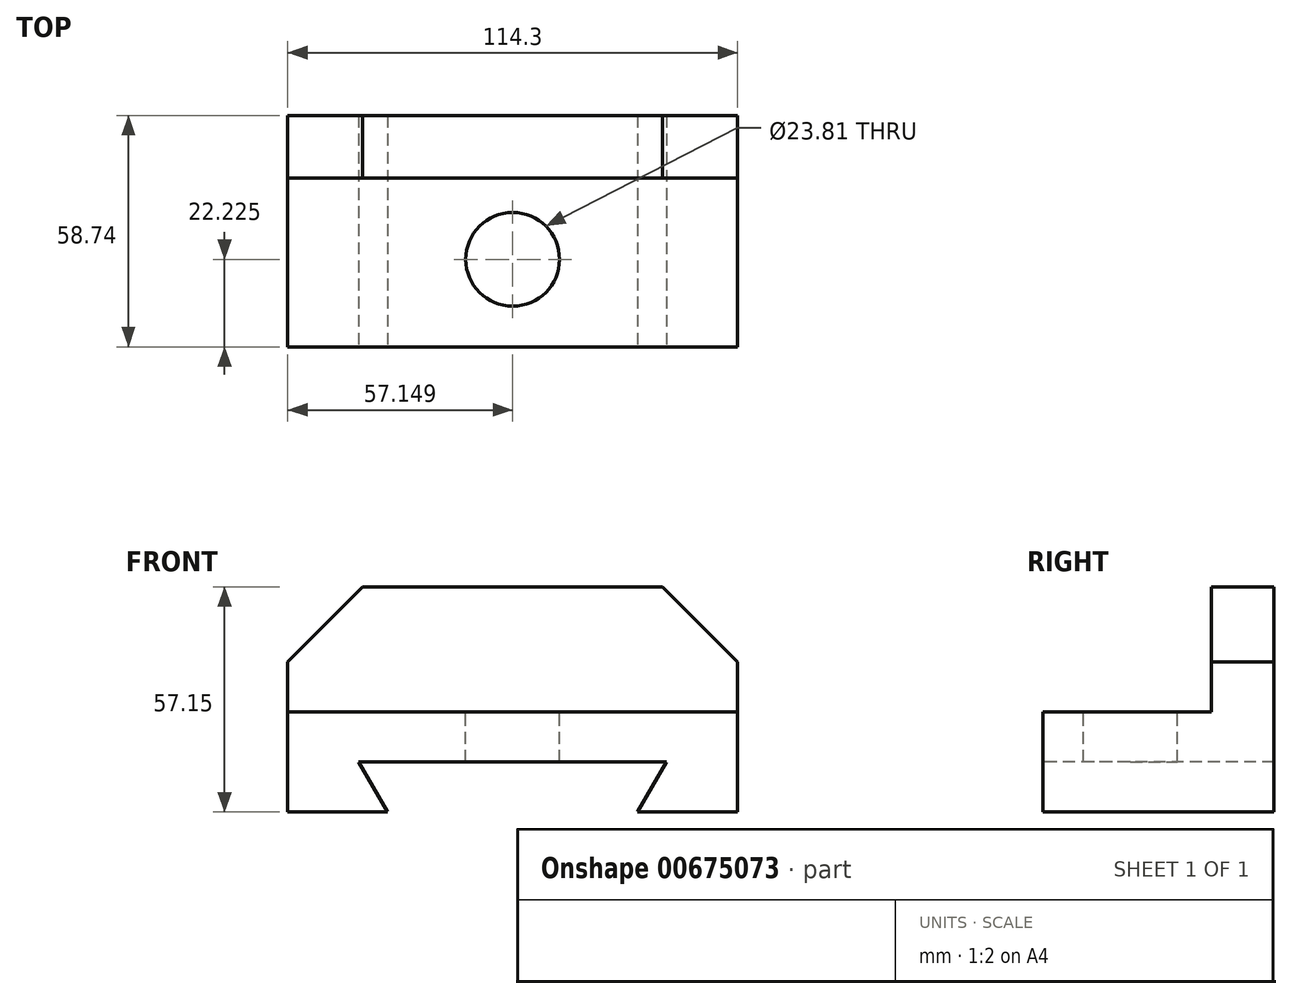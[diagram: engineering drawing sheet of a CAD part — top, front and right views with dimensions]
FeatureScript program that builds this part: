
annotation { "Feature Type Name" : "Feature", "Feature Type Description" : "" }
export const myFeature = defineFeature(function(context is Context, id is Id, definition is map)
    precondition{}
    {
        {
            var Q0;
            Q0=qCreatedBy(makeId("Front.planeOp"),FACE);
            var sketch = newSketch(context, id + "F0", { "sketchPlane" : qUnion([Q0])});
            skLineSegment(sketch, "E0.bottom", {"start": v(-52.22, -32.14) * mm, "end": v(62.08, -32.14) * mm});
            skLineSegment(sketch, "E0.top", {"start": v(-52.22, -57.54) * mm, "end": v(62.08, -57.54) * mm});
            skLineSegment(sketch, "E0.left", {"start": v(-52.22, -32.14) * mm, "end": v(-52.22, -57.54) * mm});
            skLineSegment(sketch, "E0.right", {"start": v(62.08, -32.14) * mm, "end": v(62.08, -57.54) * mm});
            skSolve(sketch);
        }
        {
            var Q0;
            Q0 = qSketchRegion(id + "F0", true);
            extrude(context, id + "F1", {"entities" : qUnion([Q0]), "oppositeDirection" : true, "depth" : 58.74 * mm, "offsetDistance" : 25.4 * mm});
        }
        {
            var Q0;
            Q0=makeQuery(id+"F1.opExtrude","SWEPT_FACE",FACE,{"disambiguationData":[OSD([sQuery(id+"F0.wireOp",EDGE,"E0.bottom")])]});
            var sketch = newSketch(context, id + "F2", { "sketchPlane" : qUnion([Q0])});
            skLineSegment(sketch, "E1.bottom", {"start": v(-52.22, 58.74) * mm, "end": v(62.08, 58.74) * mm});
            skLineSegment(sketch, "E1.top", {"start": v(-52.22, 42.86) * mm, "end": v(62.08, 42.86) * mm});
            skLineSegment(sketch, "E1.left", {"start": v(-52.22, 58.74) * mm, "end": v(-52.22, 42.86) * mm});
            skLineSegment(sketch, "E1.right", {"start": v(62.08, 58.74) * mm, "end": v(62.08, 42.86) * mm});
            skSolve(sketch);
        }
        {
            var Q0;
            Q0=makeQuery(id+"F2.imprint","IMPRINT",FACE,{"disambiguationData":[TD([[makeQuery(id+"F2.imprint","IMPRINT",EDGE,{"derivedFrom":sQuery(id+"F2.wireOp",EDGE,"E1.bottom")}),-1.0]])]});
            extrude(context, id + "F3", {"entities" : qUnion([Q0]), "operationType" : NewBodyOperationType.ADD, "depth" : 31.75 * mm, "offsetDistance" : 25.4 * mm});
        }
        {
            var Q0;
            Q0=makeQuery(id+"F3.opExtrude","SWEPT_FACE",FACE,{"disambiguationData":[OSD([sQuery(id+"F2.wireOp",EDGE,"E1.top")])]});
            var sketch = newSketch(context, id + "F4", { "sketchPlane" : qUnion([Q0])});
            skLineSegment(sketch, "E2", {"start": v(-52.22, -19.44) * mm, "end": v(-33.17, -0.4) * mm});
            skLineSegment(sketch, "E3", {"start": v(62.08, -19.44) * mm, "end": v(43.03, -0.4) * mm});
            skSolve(sketch);
        }
        {
            var Q0;
            {var subQ0=sQuery(id+"F4.wireOp",EDGE,"E2");Q0=makeQuery(id+"F4.imprint","IMPRINT",FACE,{"disambiguationData":[TD([[makeQuery(id+"F4.imprint","IMPRINT",EDGE,{"derivedFrom":subQ0}),1.0]])]});}
            var Q1;
            {var subQ0=sQuery(id+"F4.wireOp",EDGE,"E3");Q1=makeQuery(id+"F4.imprint","IMPRINT",FACE,{"disambiguationData":[TD([[makeQuery(id+"F4.imprint","IMPRINT",EDGE,{"derivedFrom":subQ0}),-1.0]])]});}
            extrude(context, id + "F5", {"entities" : qUnion([Q0, Q1]), "operationType" : NewBodyOperationType.REMOVE, "endBound" : BoundingType.THROUGH_ALL, "oppositeDirection" : true, "depth" : 25.4 * mm, "offsetDistance" : 25.4 * mm});
        }
        {
            var Q0;
            Q0=makeQuery(id+"F1.opExtrude","SWEPT_FACE",FACE,{"disambiguationData":[OSD([sQuery(id+"F0.wireOp",EDGE,"E0.bottom")])]});
            var sketch = newSketch(context, id + "F6", { "sketchPlane" : qUnion([Q0])});
            skCircle(sketch, "E4", {"center": v(4.93, 22.23) * mm, "radius": 11.9 * mm});
            skPoint(sketch, "E4.centerSnap0", {"position": v(4.93, 42.86) * mm});
            skSolve(sketch);
        }
        {
            var Q0;
            Q0=makeQuery(id+"F6.imprint","IMPRINT",FACE,{"disambiguationData":[TD([[makeQuery(id+"F6.imprint","IMPRINT",EDGE,{"derivedFrom":sQuery(id+"F6.wireOp",EDGE,"E4")}),1.0]])]});
            extrude(context, id + "F7", {"entities" : qUnion([Q0]), "operationType" : NewBodyOperationType.REMOVE, "endBound" : BoundingType.THROUGH_ALL, "oppositeDirection" : true, "depth" : 25.4 * mm, "offsetDistance" : 25.4 * mm});
        }
        {
            var Q0;
            Q0=makeQuery(id+"F1.opExtrude","CAP_FACE",FACE,{"disambiguationData":[OSD([sQuery(id+"F0.wireOp",EDGE,"E0.bottom"),sQuery(id+"F0.wireOp",EDGE,"E0.top"),sQuery(id+"F0.wireOp",EDGE,"E0.left"),sQuery(id+"F0.wireOp",EDGE,"E0.right")])],"isStart":true});
            var sketch = newSketch(context, id + "F8", { "sketchPlane" : qUnion([Q0])});
            skLineSegment(sketch, "E5", {"start": v(-34.15, -44.84) * mm, "end": v(44.01, -44.84) * mm});
            skLineSegment(sketch, "E6", {"start": v(44.01, -44.84) * mm, "end": v(36.68, -57.54) * mm});
            skLineSegment(sketch, "E7", {"start": v(-34.15, -44.84) * mm, "end": v(-26.82, -57.54) * mm});
            skSolve(sketch);
        }
        {
            var Q0;
            Q0=makeQuery(id+"F8.imprint","IMPRINT",FACE,{"disambiguationData":[TD([[makeQuery(id+"F8.imprint","IMPRINT",EDGE,{"derivedFrom":sQuery(id+"F8.wireOp",EDGE,"E5")}),-1.0]])]});
            extrude(context, id + "F9", {"entities" : qUnion([Q0]), "operationType" : NewBodyOperationType.REMOVE, "endBound" : BoundingType.THROUGH_ALL, "oppositeDirection" : true, "depth" : 25.4 * mm, "offsetDistance" : 25.4 * mm});
        }
    });
